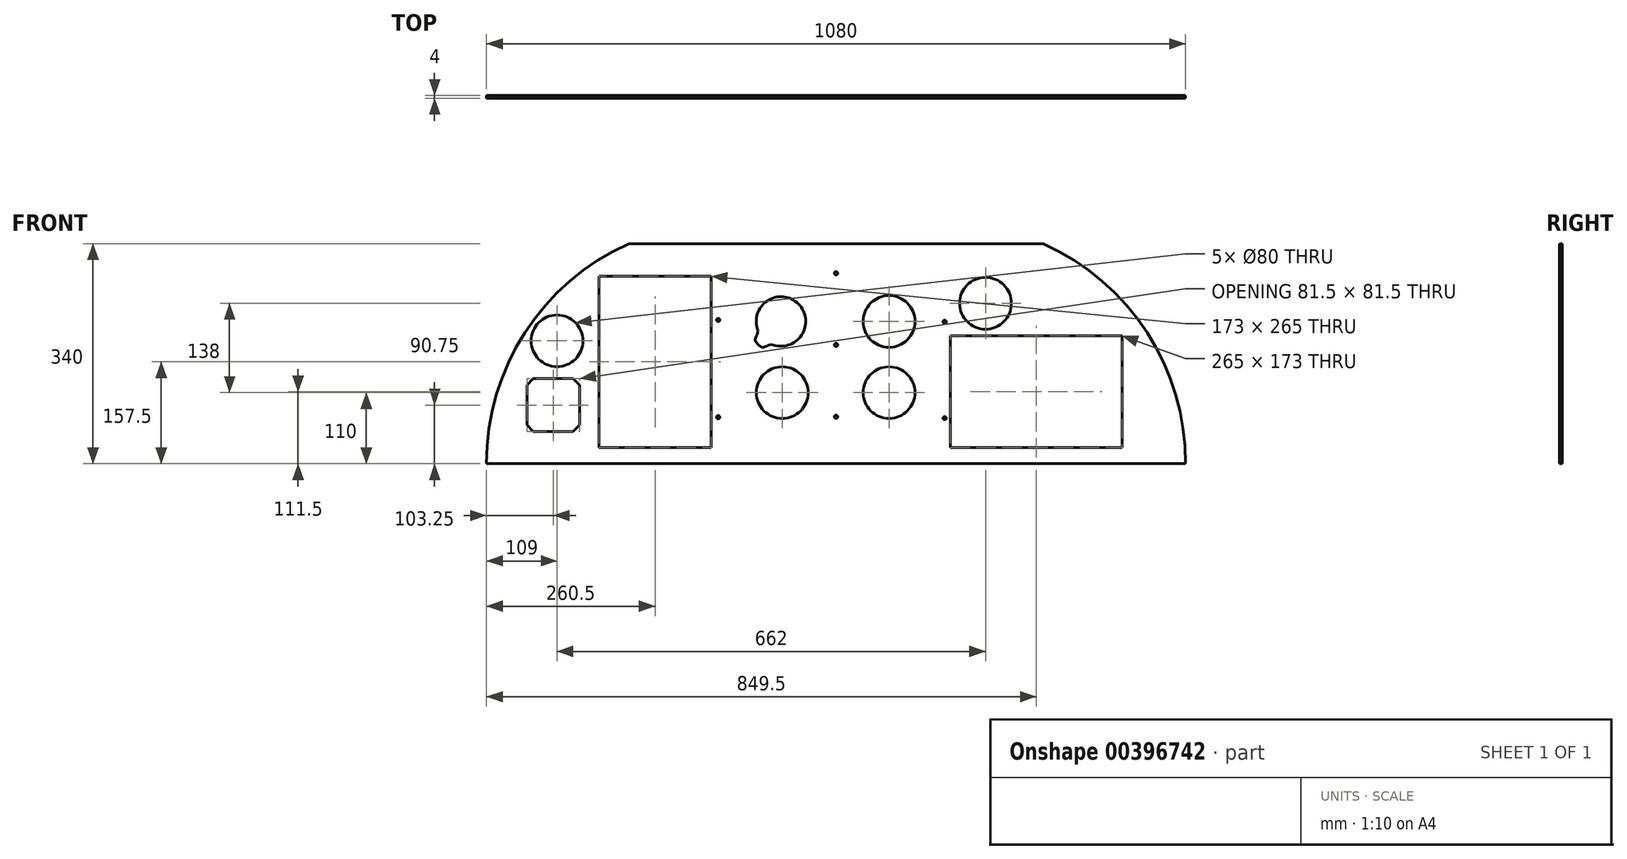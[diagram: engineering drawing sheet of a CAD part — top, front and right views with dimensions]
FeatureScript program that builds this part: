
annotation { "Feature Type Name" : "Feature", "Feature Type Description" : "" }
export const myFeature = defineFeature(function(context is Context, id is Id, definition is map)
    precondition{}
    {
        {
            var Q0;
            Q0=qCreatedBy(makeId("Front.planeOp"),FACE);
            var sketch = newSketch(context, id + "F0", { "sketchPlane" : qUnion([Q0])});
            skLineSegment(sketch, "E0", {"start": v(-540, -340) * mm, "end": v(540, -340) * mm});
            skLineSegment(sketch, "E1", {"start": v(-320, 0) * mm, "end": v(320, 0) * mm});
            skArc(sketch, "E2", {"start": v(-320, 0) * mm, "mid": v(-480.64, -137.23) * mm, "end": v(-540, -340) * mm});
            skArc(sketch, "E3", {"start": v(540, -340) * mm, "mid": v(480.64, -137.23) * mm, "end": v(320, 0) * mm});
            skSolve(sketch);
        }
        {
            var Q0;
            Q0=qSketchRegion(id+"F0",true);
            extrude(context, id + "F1", {"entities" : qUnion([Q0]), "depth" : 4 * mm});
        }
        {
            var Q0;
            Q0=makeQuery(id+"F1.opExtrude","CAP_FACE",FACE,{"disambiguationData":[OSD([sQuery(id+"F0.wireOp",EDGE,"E0"),sQuery(id+"F0.wireOp",EDGE,"E1"),sQuery(id+"F0.wireOp",EDGE,"E2"),sQuery(id+"F0.wireOp",EDGE,"E3")])],"isStart":false});
            var sketch = newSketch(context, id + "F2", { "sketchPlane" : qUnion([Q0])});
            skLineSegment(sketch, "E4", {"start": v(0, -340) * mm, "end": v(0, 0) * mm});
            skLineSegment(sketch, "E5", {"start": v(-9, -340) * mm, "end": v(0, -340) * mm});
            skLineSegment(sketch, "E6", {"start": v(0, -340) * mm, "end": v(9, -340) * mm});
            skLineSegment(sketch, "E7", {"start": v(0, -45) * mm, "end": v(-9, -45) * mm});
            skLineSegment(sketch, "E8", {"start": v(0, -45) * mm, "end": v(9, -45) * mm});
            skLineSegment(sketch, "E9", {"start": v(-9, -45) * mm, "end": v(-9, -340) * mm});
            skLineSegment(sketch, "E10", {"start": v(9, -45) * mm, "end": v(9, -340) * mm});
            skLineSegment(sketch, "E11", {"start": v(-191, -340) * mm, "end": v(-191, -80) * mm});
            skLineSegment(sketch, "E12", {"start": v(159, -340) * mm, "end": v(159, -120) * mm});
            skLineSegment(sketch, "E13", {"start": v(-191, -80) * mm, "end": v(-173, -80) * mm});
            skLineSegment(sketch, "E14", {"start": v(-173, -80) * mm, "end": v(-173, -340) * mm});
            skLineSegment(sketch, "E15", {"start": v(-191, -340) * mm, "end": v(-173, -340) * mm});
            skLineSegment(sketch, "E16", {"start": v(159, -120) * mm, "end": v(177, -120) * mm});
            skLineSegment(sketch, "E17", {"start": v(177, -120) * mm, "end": v(177, -340) * mm});
            skLineSegment(sketch, "E18", {"start": v(159, -340) * mm, "end": v(177, -340) * mm});
            skSolve(sketch);
        }
        {
            var Q0;
            {var subQ2=sQuery(id+"F2.wireOp",EDGE,"E8");Q0=makeQuery(id+"F2.imprint","IMPRINT",FACE,{"disambiguationData":[TD([[makeQuery(id+"F2.imprint","IMPRINT",EDGE,{"derivedFrom":subQ2}),1.0]])]});}
            var sketch = newSketch(context, id + "F3", { "sketchPlane" : qUnion([Q0])});
            skLineSegment(sketch, "E19.bottom", {"start": v(177, -142) * mm, "end": v(442, -142) * mm});
            skLineSegment(sketch, "E19.top", {"start": v(177, -315) * mm, "end": v(442, -315) * mm});
            skLineSegment(sketch, "E19.left", {"start": v(177, -142) * mm, "end": v(177, -315) * mm});
            skLineSegment(sketch, "E19.right", {"start": v(442, -142) * mm, "end": v(442, -315) * mm});
            skSolve(sketch);
        }
        {
            var Q0;
            Q0=makeQuery(id+"F3.imprint","IMPRINT",FACE,{"disambiguationData":[TD([[makeQuery(id+"F3.imprint","IMPRINT",EDGE,{"derivedFrom":sQuery(id+"F3.wireOp",EDGE,"E19.bottom")}),-1.0]])]});
            extrude(context, id + "F4", {"entities" : qUnion([Q0]), "operationType" : NewBodyOperationType.REMOVE, "oppositeDirection" : true, "depth" : 25 * mm});
        }
        {
            var Q0;
            Q0=qCreatedBy(makeId("Front.planeOp"),FACE);
            var sketch = newSketch(context, id + "F5", { "sketchPlane" : qUnion([Q0])});
            skLineSegment(sketch, "E20.bottom", {"start": v(-193, -315) * mm, "end": v(-366, -315) * mm});
            skLineSegment(sketch, "E20.top", {"start": v(-193, -50) * mm, "end": v(-366, -50) * mm});
            skLineSegment(sketch, "E20.left", {"start": v(-193, -315) * mm, "end": v(-193, -50) * mm});
            skLineSegment(sketch, "E20.right", {"start": v(-366, -315) * mm, "end": v(-366, -50) * mm});
            skSolve(sketch);
        }
        {
            var Q0;
            Q0=qSketchRegion(id+"F5",true);
            extrude(context, id + "F6", {"entities" : qUnion([Q0]), "operationType" : NewBodyOperationType.REMOVE, "depth" : 25 * mm});
        }
        {
            var Q0;
            Q0=qCreatedBy(makeId("Front.planeOp"),FACE);
            var sketch = newSketch(context, id + "F7", { "sketchPlane" : qUnion([Q0])});
            skCircle(sketch, "E21", {"center": v(-182.02, -268) * mm, "radius": 2.5 * mm});
            skCircle(sketch, "E22", {"center": v(-181.98, -117.82) * mm, "radius": 2.5 * mm});
            skCircle(sketch, "E23", {"center": v(0, -45.54) * mm, "radius": 2.5 * mm});
            skCircle(sketch, "E24", {"center": v(0, -156.32) * mm, "radius": 2.5 * mm});
            skCircle(sketch, "E25", {"center": v(0, -267.5) * mm, "radius": 2.5 * mm});
            skCircle(sketch, "E26", {"center": v(167.89, -120.6) * mm, "radius": 2.5 * mm});
            skCircle(sketch, "E27", {"center": v(167.89, -269.5) * mm, "radius": 2.5 * mm});
            skCircle(sketch, "E28", {"center": v(231, -92) * mm, "radius": 40 * mm});
            skCircle(sketch, "E29", {"center": v(82, -230) * mm, "radius": 40 * mm});
            skCircle(sketch, "E30", {"center": v(82, -120) * mm, "radius": 40 * mm});
            skCircle(sketch, "E31", {"center": v(-83, -230) * mm, "radius": 40 * mm});
            skCircle(sketch, "E32", {"center": v(-85, -120) * mm, "radius": 38.25 * mm});
            skSolve(sketch);
        }
        {
            var Q0;
            Q0=qSketchRegion(id+"F7",true);
            extrude(context, id + "F8", {"entities" : qUnion([Q0]), "operationType" : NewBodyOperationType.REMOVE, "oppositeDirection" : true, "depth" : 25 * mm});
        }
        {
            var Q0;
            Q0=qSketchRegion(id+"F7",true);
            extrude(context, id + "F9", {"entities" : qUnion([Q0]), "operationType" : NewBodyOperationType.REMOVE, "endBound" : BoundingType.SYMMETRIC, "oppositeDirection" : true, "depth" : 25 * mm});
        }
        {
            var Q0;
            {var subQ1=sQuery(id+"F2.wireOp",EDGE,"E7");Q0=makeQuery(id+"F2.imprint","IMPRINT",FACE,{"disambiguationData":[TD([[makeQuery(id+"F2.imprint","IMPRINT",EDGE,{"derivedFrom":subQ1}),-1.0]])]});}
            var sketch = newSketch(context, id + "F10", { "sketchPlane" : qUnion([Q0])});
            skLineSegment(sketch, "E33", {"start": v(-123.25, -120) * mm, "end": v(-46.75, -120) * mm, "construction": true});
            skPoint(sketch, "E34", {"position": v(-85, -120) * mm});
            skLineSegment(sketch, "E35", {"start": v(-85, -120) * mm, "end": v(-139.53, -174.53) * mm, "construction": true});
            skPoint(sketch, "E36", {"position": v(-120.49, -155.49) * mm});
            skLineSegment(sketch, "E37", {"start": v(-120.49, -134.27) * mm, "end": v(-99.27, -155.49) * mm, "construction": true});
            skPoint(sketch, "E38", {"position": v(-109.88, -144.88) * mm});
            skPoint(sketch, "E39", {"position": v(-125.08, -148.06) * mm});
            skPoint(sketch, "E40", {"position": v(-113.06, -160.08) * mm});
            skFitSpline(sketch, "E41", {"points": [v(-120.49, -134.27) * mm, v(-125.08, -148.06) * mm, v(-120.49, -155.49) * mm, v(-113.06, -160.08) * mm, v(-99.27, -155.49) * mm], "startDerivative": vector(-6.17, -77.7) * mm, "endDerivative": vector(68.34, 7.08) * mm});
            skLineSegment(sketch, "E42", {"start": v(-120.49, -134.27) * mm, "end": v(-99.27, -155.49) * mm});
            skSolve(sketch);
        }
        {
            var Q0;
            {var subQ2=sQuery(id+"F2.wireOp",EDGE,"E7");Q0=makeQuery(id+"F10.imprint","IMPRINT",FACE,{"disambiguationData":[TD([[makeQuery(id+"F10.imprint","IMPRINT",EDGE,{"derivedFrom":makeQuery(id+"F2.imprint","IMPRINT",EDGE,{"derivedFrom":subQ2})}),-1.0]])]});}
            var sketch = newSketch(context, id + "F11", { "sketchPlane" : qUnion([Q0])});
            skSolve(sketch);
        }
        {
            var Q0;
            Q0=makeQuery(id+"F10.imprint","IMPRINT",FACE,{"disambiguationData":[TD([[makeQuery(id+"F10.imprint","IMPRINT",EDGE,{"derivedFrom":sQuery(id+"F10.wireOp",EDGE,"E41")}),1.0]])]});
            extrude(context, id + "F12", {"entities" : qUnion([Q0]), "operationType" : NewBodyOperationType.REMOVE, "endBound" : BoundingType.THROUGH_ALL, "oppositeDirection" : true, "depth" : 25 * mm});
        }
        {
            var Q0;
            Q0=makeQuery(id+"F11.imprint","IMPRINT",FACE,{"disambiguationData":[TD([[makeQuery(id+"F11.imprint","IMPRINT",EDGE,{"derivedFrom":makeQuery(id+"F10.imprint","IMPRINT",EDGE,{"derivedFrom":sQuery(id+"F10.wireOp",EDGE,"E41")})}),-1.0]])]});
            var sketch = newSketch(context, id + "F13", { "sketchPlane" : qUnion([Q0])});
            skCircle(sketch, "E43", {"center": v(-431, -150) * mm, "radius": 40 * mm});
            skLineSegment(sketch, "E44", {"start": v(-396, -280) * mm, "end": v(-406, -290) * mm});
            skLineSegment(sketch, "E45", {"start": v(-477.5, -280) * mm, "end": v(-467.5, -290) * mm});
            skLineSegment(sketch, "E46", {"start": v(-467.5, -208.5) * mm, "end": v(-477.5, -218.5) * mm});
            skLineSegment(sketch, "E47", {"start": v(-406, -208.5) * mm, "end": v(-396, -218.5) * mm});
            skLineSegment(sketch, "E48", {"start": v(-406, -290) * mm, "end": v(-396, -280) * mm});
            skLineSegment(sketch, "E49", {"start": v(-396, -218.5) * mm, "end": v(-406, -208.5) * mm});
            skLineSegment(sketch, "E50", {"start": v(-467.5, -208.5) * mm, "end": v(-406, -208.5) * mm});
            skLineSegment(sketch, "E51", {"start": v(-477.5, -218.5) * mm, "end": v(-477.5, -280) * mm});
            skLineSegment(sketch, "E52", {"start": v(-467.5, -290) * mm, "end": v(-406, -290) * mm});
            skLineSegment(sketch, "E53", {"start": v(-396, -280) * mm, "end": v(-396, -218.5) * mm});
            skSolve(sketch);
        }
        {
            var Q0;
            Q0=qSketchRegion(id+"F13",true);
            extrude(context, id + "F14", {"entities" : qUnion([Q0]), "operationType" : NewBodyOperationType.REMOVE, "oppositeDirection" : true, "depth" : 25 * mm});
        }
        {
            var Q0;
            Q0=makeQuery(id+"F11.imprint","IMPRINT",FACE,{"disambiguationData":[TD([[makeQuery(id+"F11.imprint","IMPRINT",EDGE,{"derivedFrom":makeQuery(id+"F10.imprint","IMPRINT",EDGE,{"derivedFrom":sQuery(id+"F10.wireOp",EDGE,"E41")})}),-1.0]])]});
            var sketch = newSketch(context, id + "F15", { "sketchPlane" : qUnion([Q0])});
            skCircle(sketch, "E54", {"center": v(-181.97, -117.78) * mm, "radius": 2.49 * mm});
            skPoint(sketch, "E54.first.point", {"position": v(-180.44, -115.82) * mm});
            skPoint(sketch, "E54.second.point", {"position": v(-184.45, -117.59) * mm});
            skPoint(sketch, "E54.third.point", {"position": v(-181.23, -120.15) * mm});
            skCircle(sketch, "E55", {"center": v(-182.03, -268.01) * mm, "radius": 2.48 * mm});
            skPoint(sketch, "E55.first.point", {"position": v(-180.39, -269.87) * mm});
            skPoint(sketch, "E55.second.point", {"position": v(-182.08, -265.53) * mm});
            skPoint(sketch, "E55.third.point", {"position": v(-184.46, -267.5) * mm});
            skCircle(sketch, "E56", {"center": v(0, -267.5) * mm, "radius": 2.5 * mm});
            skPoint(sketch, "E56.first.point", {"position": v(2.5, -267.5) * mm});
            skPoint(sketch, "E56.second.point", {"position": v(-0.66, -265.1) * mm});
            skPoint(sketch, "E56.third.point", {"position": v(-2.38, -266.73) * mm});
            skCircle(sketch, "E57", {"center": v(0, -156.32) * mm, "radius": 2.5 * mm});
            skPoint(sketch, "E57.first.point", {"position": v(2.14, -155.04) * mm});
            skPoint(sketch, "E57.second.point", {"position": v(-1.93, -154.74) * mm});
            skPoint(sketch, "E57.third.point", {"position": v(-2.29, -157.32) * mm});
            skCircle(sketch, "E58", {"center": v(-0.02, -45.53) * mm, "radius": 2.49 * mm});
            skPoint(sketch, "E58.first.point", {"position": v(1.91, -43.96) * mm});
            skPoint(sketch, "E58.second.point", {"position": v(-2.08, -44.14) * mm});
            skPoint(sketch, "E58.third.point", {"position": v(-0.62, -47.94) * mm});
            skCircle(sketch, "E59", {"center": v(167.88, -269.48) * mm, "radius": 2.45 * mm});
            skPoint(sketch, "E59.first.point", {"position": v(170.33, -269.55) * mm});
            skPoint(sketch, "E59.second.point", {"position": v(167.54, -267.06) * mm});
            skPoint(sketch, "E59.third.point", {"position": v(165.5, -270.07) * mm});
            skCircle(sketch, "E60", {"center": v(167.87, -120.6) * mm, "radius": 2.5 * mm});
            skPoint(sketch, "E60.first.point", {"position": v(169.27, -118.52) * mm});
            skPoint(sketch, "E60.second.point", {"position": v(165.41, -120.16) * mm});
            skPoint(sketch, "E60.third.point", {"position": v(167.37, -123.05) * mm});
            skSolve(sketch);
        }
        {
            var Q0;
            Q0 = qSketchRegion(id + "F15", true);
            extrude(context, id + "F16", {"entities" : qUnion([Q0]), "oppositeDirection" : true, "depth" : 4 * mm});
        }
    });
